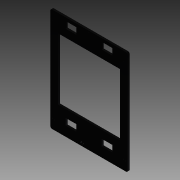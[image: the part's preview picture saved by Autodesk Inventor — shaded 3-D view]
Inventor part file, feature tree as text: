
AUTODESK INVENTOR PART (.ipt)
format: ipt  version: 2013 (Build 170138000, 138)  size: 209,408 bytes
history: native  units: in
note: dims shown in document units (in); Inventor stores cm internally (conversion verified against a paired STEP export)
features: extrude x7, sketch x7, reference x7, fillet x1
ambient origin geometry x8: Origin, YZ Plane, XZ Plane, XY Plane, X Axis, Y Axis, Z Axis, Center Point
bodies: Solid1 (feature_tree)
feature tree (22):
  extrude  "Extrusion1"  Depth=8.0in
  extrude  "Extrusion2"  Depth=0.255in TaperAngle=0.0deg
  extrude  "Extrusion3"  Depth=1.378in
  extrude  "Extrusion4"  Depth=1.0in TaperAngle=0.0deg
  extrude  "Extrusion5"  Depth=1.0in TaperAngle=0.0deg
  extrude  "Extrusion6"  Depth=1.5in
  extrude  "Extrusion7"  Depth=1.0in TaperAngle=0.0deg
  fillet  "Fillet1"  Radius=0.1875in
  sketch  "Sketch1"  dims[d0=0.255in d1=0.0in d2=8.0in]
  reference  "Reference1"
  sketch  "Sketch2"  dims[d4=3.1102in d5=0.255in d6=0.0in]
  sketch  "Sketch3"  dims[d7=0.8661in d9=1.378in]
  reference  "Reference2"
  reference  "Reference3"
  sketch  "Sketch4"  dims[d10=1.9685in d11=1.0in d12=0.0in]
  reference  "Reference4"
  reference  "Reference5"
  sketch  "Sketch5"  dims[d13=1.0in d14=0.0in d15=1.0in d16=0.0in]
  reference  "Reference6"
  sketch  "Sketch6"  dims[d17=1.0in d18=0.0in d19=1.5in]
  reference  "Reference7"
  sketch  "Sketch7"  dims[d21=0.375in d22=1.0in d23=0.0in d24=0.1875in]
